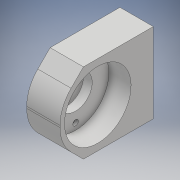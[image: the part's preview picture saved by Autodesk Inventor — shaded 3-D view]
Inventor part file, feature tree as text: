
AUTODESK INVENTOR PART (.ipt)
format: ipt  version: 2018 (Build 220112000, 112)  size: 163,328 bytes
history: native  units: mm
features: sketch x6, extrude x4, hole x2, fillet x1
ambient origin geometry x8: Origin, YZ Plane, XZ Plane, XY Plane, X Axis, Y Axis, Z Axis, Center Point
bodies: Solid1 (feature_tree)
feature tree (13):
  extrude  "Extrusion1"  Depth=17.0mm
  extrude  "Extrusion2"  Depth=18.0mm
  extrude  "Extrusion3"  Depth=15.0mm TaperAngle=0.0deg
  extrude  "Extrusion4"  Depth=17.0mm
  hole  "Hole1"  [1 undecoded]
  hole  "Hole2"  [1 undecoded]
  fillet  "Fillet1"  [1 undecoded]
  sketch  "Sketch1"  dims[d0=30.0mm d1=17.0mm]
  sketch  "Sketch2"  dims[d2=25.0mm d3=18.0mm]
  sketch  "Sketch3"  dims[d5=135.0deg d6=15.0mm d7=0.0mm]
  sketch  "Sketch4"  dims[d8=30.0mm d9=17.0mm]
  sketch  "Sketch5"  dims[d10=10.0mm d11=0.0mm d12=15.0mm]
  sketch  "Sketch6"  dims[d13=4.0mm d14=0.0mm d15=4.5mm d16=0.0mm d17=0.0mm d18=24.0mm d19=2.459mm d20=6.0mm d21=6.0mm d22=3.5mm d23=90.0deg d24=8.0mm d25=20.594885mm d26=12.5mm d27=6.0mm d28=4.917mm d29=12.0mm d30=4.0mm d31=2.0mm d32=90.0deg d33=5.0mm d34=20.594885mm d35=17.0mm]
note: 3 required parameter values undecoded (feature->parameter linkage not recoverable at this tier; creation-order binding heuristic only, values carry confidence <= 0.55)
